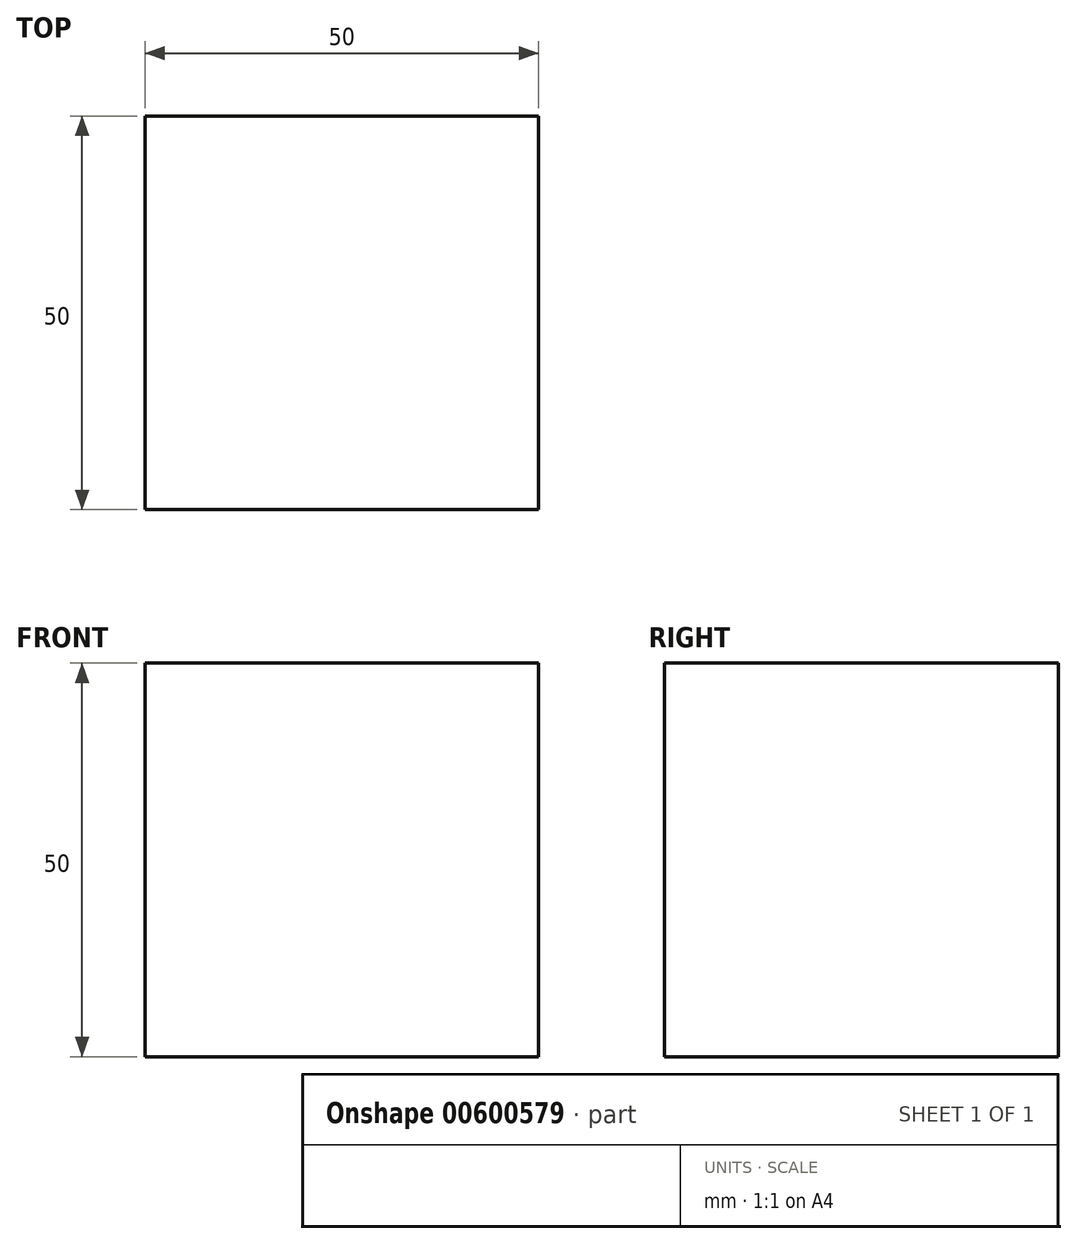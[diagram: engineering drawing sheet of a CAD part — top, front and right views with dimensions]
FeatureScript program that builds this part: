
annotation { "Feature Type Name" : "Feature", "Feature Type Description" : "" }
export const myFeature = defineFeature(function(context is Context, id is Id, definition is map)
    precondition{}
    {
        {
            var Q0;
            Q0=qCreatedBy(makeId("Top.planeOp"),FACE);
            var sketch = newSketch(context, id + "F0", { "sketchPlane" : qUnion([Q0])});
            skLineSegment(sketch, "E0.bottom", {"start": v(11.43, -20.23) * mm, "end": v(61.43, -20.23) * mm});
            skLineSegment(sketch, "E0.top", {"start": v(11.43, 29.77) * mm, "end": v(61.43, 29.77) * mm});
            skLineSegment(sketch, "E0.left", {"start": v(11.43, -20.23) * mm, "end": v(11.43, 29.77) * mm});
            skLineSegment(sketch, "E0.right", {"start": v(61.43, -20.23) * mm, "end": v(61.43, 29.77) * mm});
            skPoint(sketch, "E0.middle", {"position": v(36.43, 4.77) * mm});
            skSolve(sketch);
        }
        {
            var Q0;
            Q0 = qSketchRegion(id + "F0", true);
            extrude(context, id + "F1", {"entities" : qUnion([Q0]), "depth" : 50 * mm, "offsetDistance" : 25 * mm});
        }
    });
